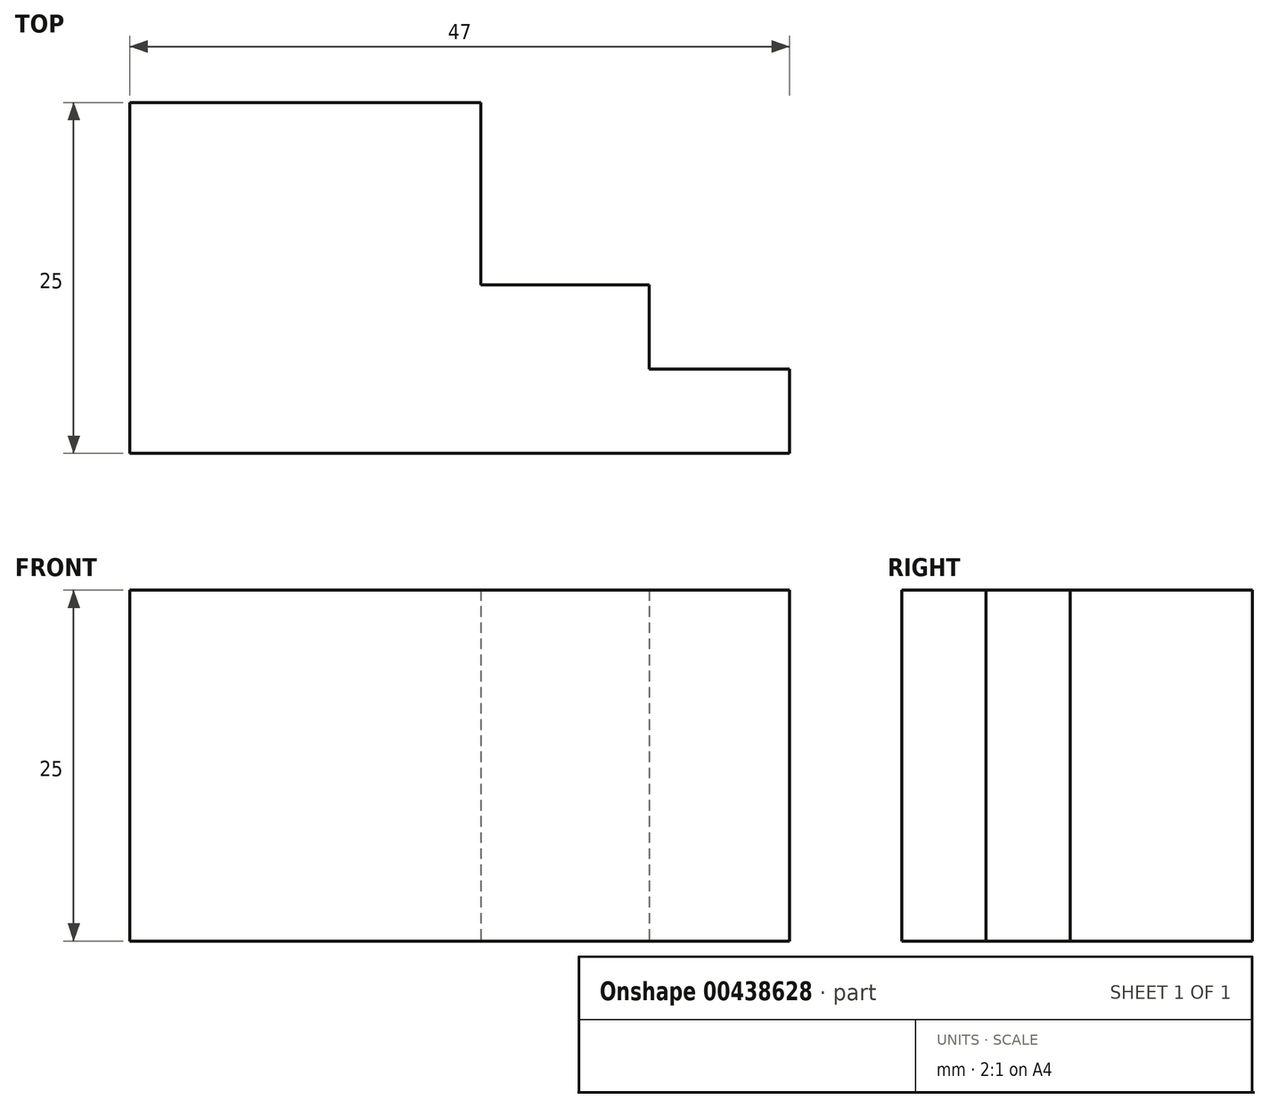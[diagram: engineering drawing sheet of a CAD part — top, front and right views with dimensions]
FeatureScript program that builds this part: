
annotation { "Feature Type Name" : "Feature", "Feature Type Description" : "" }
export const myFeature = defineFeature(function(context is Context, id is Id, definition is map)
    precondition{}
    {
        {
            var Q0;
            Q0=qCreatedBy(makeId("Top.planeOp"),FACE);
            var sketch = newSketch(context, id + "F0", { "sketchPlane" : qUnion([Q0])});
            skLineSegment(sketch, "E0.bottom", {"start": v(-32.03, 25) * mm, "end": v(-7.03, 25) * mm});
            skLineSegment(sketch, "E0.top", {"start": v(-32.03, 0) * mm, "end": v(-7.03, 0) * mm});
            skLineSegment(sketch, "E0.left", {"start": v(-32.03, 25) * mm, "end": v(-32.03, 0) * mm});
            skLineSegment(sketch, "E0.right", {"start": v(-7.03, 25) * mm, "end": v(-7.03, 0) * mm});
            skLineSegment(sketch, "E1.bottom", {"start": v(-7.03, 12) * mm, "end": v(4.97, 12) * mm});
            skLineSegment(sketch, "E1.top", {"start": v(-7.03, 0) * mm, "end": v(4.97, 0) * mm});
            skLineSegment(sketch, "E1.left", {"start": v(-7.03, 12) * mm, "end": v(-7.03, 0) * mm});
            skLineSegment(sketch, "E1.right", {"start": v(4.97, 12) * mm, "end": v(4.97, 0) * mm});
            skLineSegment(sketch, "E2.bottom", {"start": v(4.97, 6) * mm, "end": v(14.97, 6) * mm});
            skLineSegment(sketch, "E2.top", {"start": v(4.97, 0) * mm, "end": v(14.97, 0) * mm});
            skLineSegment(sketch, "E2.left", {"start": v(4.97, 6) * mm, "end": v(4.97, 0) * mm});
            skLineSegment(sketch, "E2.right", {"start": v(14.97, 6) * mm, "end": v(14.97, 0) * mm});
            skSolve(sketch);
        }
        {
            var Q0;
            Q0=makeQuery(id+"F0.imprint","IMPRINT",FACE,{"disambiguationData":[TD([[makeQuery(id+"F0.imprint","IMPRINT",EDGE,{"derivedFrom":sQuery(id+"F0.wireOp",EDGE,"E0.bottom")}),-1.0]])]});
            var Q1;
            Q1=makeQuery(id+"F0.imprint","IMPRINT",FACE,{"disambiguationData":[TD([[makeQuery(id+"F0.imprint","IMPRINT",EDGE,{"derivedFrom":sQuery(id+"F0.wireOp",EDGE,"E1.bottom")}),-1.0]])]});
            var Q2;
            Q2=makeQuery(id+"F0.imprint","IMPRINT",FACE,{"disambiguationData":[TD([[makeQuery(id+"F0.imprint","IMPRINT",EDGE,{"derivedFrom":sQuery(id+"F0.wireOp",EDGE,"E2.bottom")}),-1.0]])]});
            extrude(context, id + "F1", {"entities" : qUnion([Q0, Q1, Q2]), "depth" : 25 * mm});
        }
    });
